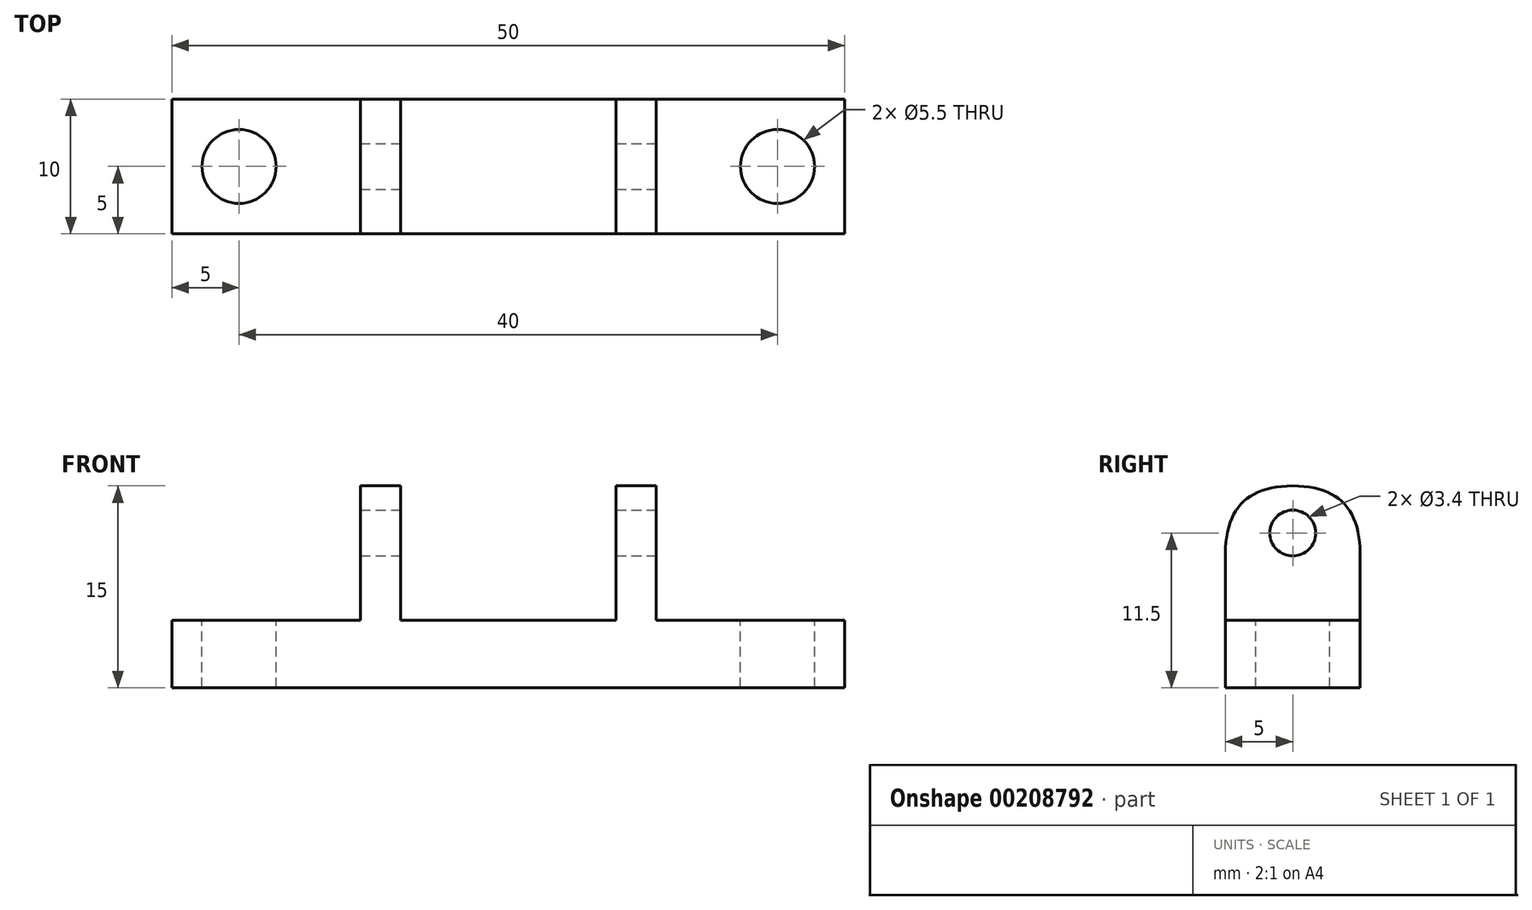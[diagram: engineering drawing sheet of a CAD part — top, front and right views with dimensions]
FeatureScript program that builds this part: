
annotation { "Feature Type Name" : "Feature", "Feature Type Description" : "" }
export const myFeature = defineFeature(function(context is Context, id is Id, definition is map)
    precondition{}
    {
        {
            var Q0;
            Q0=qCreatedBy(makeId("Top.planeOp"),FACE);
            var sketch = newSketch(context, id + "F0", { "sketchPlane" : qUnion([Q0])});
            skLineSegment(sketch, "E0.bottom", {"start": v(25, -5) * mm, "end": v(-25, -5) * mm});
            skLineSegment(sketch, "E0.top", {"start": v(25, 5) * mm, "end": v(-25, 5) * mm});
            skLineSegment(sketch, "E0.left", {"start": v(25, -5) * mm, "end": v(25, 5) * mm});
            skLineSegment(sketch, "E0.right", {"start": v(-25, -5) * mm, "end": v(-25, 5) * mm});
            skPoint(sketch, "E0.middle", {"position": v(0, 0) * mm});
            skLineSegment(sketch, "E1", {"start": v(-20, 0) * mm, "end": v(20, 0) * mm, "construction": true});
            skPoint(sketch, "E1.endSnap0", {"position": v(25, 0) * mm});
            skSolve(sketch);
        }
        {
            var Q0;
            Q0 = qSketchRegion(id + "F0", true);
            var Q1;
            Q1 = qConstructionFilter(qBodyType(qCreatedBy(id + "F0" ,EDGE), BodyType.WIRE), ConstructionObject.NO);
            extrude(context, id + "F1", {"entities" : qUnion([Q0]), "surfaceEntities" : qUnion([Q1]), "depth" : 5 * mm, "offsetDistance" : 25 * mm});
        }
        {
            var Q0;
            Q0=sQuery(id+"F0.wireOp",VERTEX,"E1.start");
            var Q1;
            Q1=sQuery(id+"F0.wireOp",VERTEX,"E1.end");
            var Q2;
            Q2=makeQuery(id+"F1.opExtrude","SWEPT_BODY",BODY,{"disambiguationData":[OSD([sQuery(id+"F0.wireOp",EDGE,"E0.bottom"),sQuery(id+"F0.wireOp",EDGE,"E0.top"),sQuery(id+"F0.wireOp",EDGE,"E0.left"),sQuery(id+"F0.wireOp",EDGE,"E0.right")])]});
            hole(context, id + "F2", {"style" : HoleStyle.SIMPLE, "endStyle" : HoleEndStyle.THROUGH, "oppositeDirection" : true, "standardTappedOrClearance" : lookupTablePath({ "standard" : "ISO", "fit" : "Normal", "size" : "M5", "type" : "Clearance" }), "standardBlindInLast" : lookupTablePath({ "fit" : "Standard", "standard" : "ISO", "size" : "M5", "type" : "Clearance" }), "holeDiameter" : 5.5 * mm, "majorDiameter" : 5 * mm, "isTappedThrough" : true, "tappedDepth" : 12 * mm, "tapClearance" : 3, "locations" : qUnion([Q0, Q1]), "scope" : qUnion([Q2])});
        }
        {
            var Q0;
            Q0=makeQuery(id+"F1.opExtrude","CAP_FACE",FACE,{"disambiguationData":[OSD([sQuery(id+"F0.wireOp",EDGE,"E0.bottom"),sQuery(id+"F0.wireOp",EDGE,"E0.top"),sQuery(id+"F0.wireOp",EDGE,"E0.left"),sQuery(id+"F0.wireOp",EDGE,"E0.right")])],"isStart":false});
            var sketch = newSketch(context, id + "F3", { "sketchPlane" : qUnion([Q0])});
            skLineSegment(sketch, "E2", {"start": v(-8, 0) * mm, "end": v(8, 0) * mm, "construction": true});
            skLineSegment(sketch, "E3.bottom", {"start": v(-8, -5) * mm, "end": v(-11, -5) * mm});
            skLineSegment(sketch, "E3.top", {"start": v(-8, 5) * mm, "end": v(-11, 5) * mm});
            skLineSegment(sketch, "E3.left", {"start": v(-8, -5) * mm, "end": v(-8, 5) * mm});
            skLineSegment(sketch, "E3.right", {"start": v(-11, -5) * mm, "end": v(-11, 5) * mm});
            skLineSegment(sketch, "E4.bottom", {"start": v(8, -5) * mm, "end": v(11, -5) * mm});
            skLineSegment(sketch, "E4.top", {"start": v(8, 5) * mm, "end": v(11, 5) * mm});
            skLineSegment(sketch, "E4.left", {"start": v(8, -5) * mm, "end": v(8, 5) * mm});
            skLineSegment(sketch, "E4.right", {"start": v(11, -5) * mm, "end": v(11, 5) * mm});
            skSolve(sketch);
        }
        {
            var Q0;
            Q0 = qSketchRegion(id + "F3", true);
            extrude(context, id + "F4", {"entities" : qUnion([Q0]), "operationType" : NewBodyOperationType.ADD, "depth" : 10 * mm, "offsetDistance" : 25 * mm});
        }
        {
            var Q0;
            Q0=makeQuery(id+"F4.opExtrude","CAP_EDGE",EDGE,{"disambiguationData":[OSD([sQuery(id+"F3.wireOp",EDGE,"E3.bottom")])],"isStart":false});
            var Q1;
            Q1=makeQuery(id+"F4.opExtrude","CAP_EDGE",EDGE,{"disambiguationData":[OSD([sQuery(id+"F3.wireOp",EDGE,"E3.top")])],"isStart":false});
            var Q2;
            Q2=makeQuery(id+"F4.opExtrude","CAP_EDGE",EDGE,{"disambiguationData":[OSD([sQuery(id+"F3.wireOp",EDGE,"E4.bottom")])],"isStart":false});
            var Q3;
            Q3=makeQuery(id+"F4.opExtrude","CAP_EDGE",EDGE,{"disambiguationData":[OSD([sQuery(id+"F3.wireOp",EDGE,"E4.top")])],"isStart":false});
            fillet(context, id + "F5", {"entities" : qUnion([Q0, Q1, Q2, Q3]), "radius" : 5 * mm, "tangentPropagation" : true, "rho" : 0.5, "crossSection" : FilletCrossSection.CONIC, "allowEdgeOverflow" : false});
        }
        {
            var Q0;
            Q0=makeQuery(id+"F4.opExtrude","SWEPT_FACE",FACE,{"disambiguationData":[OSD([sQuery(id+"F3.wireOp",EDGE,"E3.right")])]});
            var sketch = newSketch(context, id + "F6", { "sketchPlane" : qUnion([Q0])});
            skPoint(sketch, "E5", {"position": v(0, 11.5) * mm});
            skSolve(sketch);
        }
        {
            var Q0;
            Q0=sQuery(id+"F6.wireOp",VERTEX,"E5");
            var Q1;
            Q1=makeQuery(id+"F1.opExtrude","SWEPT_BODY",BODY,{"disambiguationData":[OSD([sQuery(id+"F0.wireOp",EDGE,"E0.bottom"),sQuery(id+"F0.wireOp",EDGE,"E0.top"),sQuery(id+"F0.wireOp",EDGE,"E0.left"),sQuery(id+"F0.wireOp",EDGE,"E0.right")])]});
            hole(context, id + "F7", {"style" : HoleStyle.SIMPLE, "endStyle" : HoleEndStyle.THROUGH, "standardTappedOrClearance" : lookupTablePath({ "fit" : "Normal", "standard" : "ISO", "size" : "M3", "type" : "Clearance" }), "standardBlindInLast" : lookupTablePath({ "fit" : "Normal", "standard" : "ISO", "engagement" : "75%", "pitch" : "0.5 mm", "size" : "M3", "type" : "Clearance & tapped" }), "holeDiameter" : 3.4 * mm, "majorDiameter" : 5 * mm, "isTappedThrough" : true, "tappedDepth" : 12 * mm, "tapClearance" : 3, "locations" : qUnion([Q0]), "scope" : qUnion([Q1])});
        }
    });
